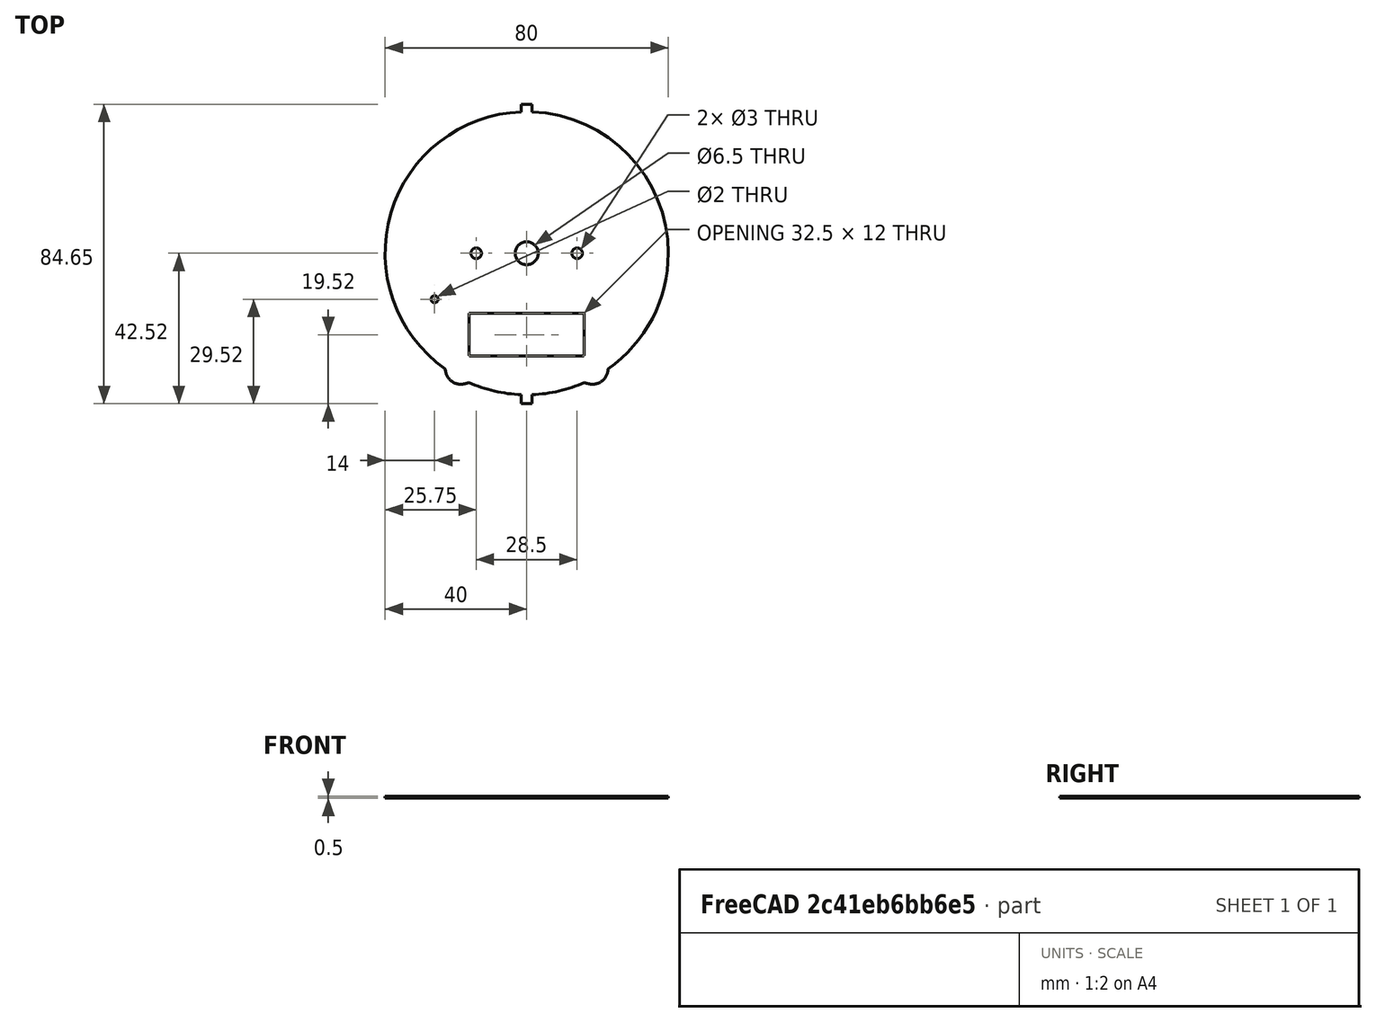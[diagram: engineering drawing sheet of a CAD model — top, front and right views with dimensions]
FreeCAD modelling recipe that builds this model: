
FCSTD DOCUMENT  (FreeCAD 1.0R39285 (Git))
Label: Tach_Face_Reference_CAD_Model
License: All rights reserved
LicenseURL: http://en.wikipedia.org/wiki/All_rights_reserved
objects: TechDraw::DrawViewDimension×17, Sketcher::SketchObject×6, PartDesign::Pad×3, PartDesign::Pocket×3, TechDraw::DrawProjGroupItem×2, Image::ImagePlane×1, PartDesign::Body×1, TechDraw::DrawSVGTemplate×1, TechDraw::DrawProjGroup×1, TechDraw::DrawViewAnnotation×1, TechDraw::DrawPage×1
note: 57 computed .brp shape members not serialized (recipe doc carries the construction recipe); baked Part::Feature solids carry a one-line shape summary decoded from their .brp

FEATURE [Sketcher::SketchObject] Sketch  label="Square Hole"
  ArcFitTolerance = 1e-06
  AttachmentSupport = -> [XY_Plane]
  FullyConstrained = true
  MakeInternals = false
  MapMode = 5
  sketch-geometry (5):
    g0: LineSegment StartX=-16.25 StartY=-29 StartZ=0 EndX=16.25 EndY=-29 EndZ=0
    g1: LineSegment StartX=16.25 StartY=-29 StartZ=0 EndX=16.25 EndY=-17 EndZ=0
    g2: LineSegment StartX=16.25 StartY=-17 StartZ=0 EndX=-16.25 EndY=-17 EndZ=0
    g3: LineSegment StartX=-16.25 StartY=-17 StartZ=0 EndX=-16.25 EndY=-29 EndZ=0
    g4: LineSegment [constr] StartX=0 StartY=0 StartZ=0 EndX=0 EndY=-17 EndZ=0
  constraints (14):
    c: Coincident(g1,g0)
    c: Vertical(g1)
    c: Coincident(g2,g1)
    c: Horizontal(g2)
    c: Coincident(g3,g2)
    c: Coincident(g3,g0)
    c: Vertical(g3)
    c: Horizontal(g0)
    c: Coincident(g4,g-1)
    c: DistanceY(g4,g4) = 17
    c: PointOnObject(g4,g2)
    c: Symmetric(g2,g1,g4)
    c: DistanceX(g0,g0) = 32.5
    c: DistanceY(g1,g1) = 12
FEATURE [Sketcher::SketchObject] Sketch001  label="Main Body"
  ArcFitTolerance = 1e-06
  AttachmentSupport = -> [XY_Plane]
  FullyConstrained = true
  MakeInternals = false
  MapMode = 5
  sketch-geometry (1):
    g0: Circle CenterX=0 CenterY=0 CenterZ=0 NormalX=0 NormalY=0 NormalZ=1 AngleXU=0 Radius=40
  constraints (2):
    c: Coincident(g-1,g0)
    c: Diameter(g0) = 80
FEATURE [Image::ImagePlane] Tach_Face_Reference_Image
  Placement = pos=(-3,-9,0) rot=(0,0,1;0rad)
  XSize = 229.908
  YSize = 172.431
FEATURE [PartDesign::Pad] Pad
  Direction = (0,0,1)
  Length = 0.5
  Length2 = 10
  Profile = -> Sketch001
  ReferenceAxis = -> Sketch001 [N_Axis]
  Suppressed = false
  Type = 0
FEATURE [PartDesign::Pocket] Pocket  label="Square_Hole"
  BaseFeature = -> Pad
  Direction = (0,0,-1)
  Length = 5
  Length2 = 5
  Profile = -> Sketch
  ReferenceAxis = -> Sketch [N_Axis]
  Reversed = true
  Suppressed = false
  Type = 1
FEATURE [Sketcher::SketchObject] Sketch002
  ArcFitTolerance = 1e-06
  AttachmentSupport = -> [XY_Plane]
  FullyConstrained = true
  MakeInternals = false
  MapMode = 5
  sketch-geometry (5):
    g0: Circle CenterX=0 CenterY=0 CenterZ=0 NormalX=0 NormalY=0 NormalZ=1 AngleXU=0 Radius=3.25
    g1: LineSegment [constr] StartX=0 StartY=0 StartZ=0 EndX=14.25 EndY=0 EndZ=0
    g2: Circle CenterX=14.25 CenterY=0 CenterZ=0 NormalX=0 NormalY=0 NormalZ=1 AngleXU=0 Radius=1.5
    g3: LineSegment [constr] StartX=0 StartY=0 StartZ=0 EndX=-14.25 EndY=0 EndZ=0
    g4: Circle CenterX=-14.25 CenterY=0 CenterZ=0 NormalX=0 NormalY=0 NormalZ=1 AngleXU=0 Radius=1.5
  constraints (12):
    c: Coincident(g0,g-1)
    c: Diameter(g0) = 6.5
    c: Coincident(g1,g0)
    c: PointOnObject(g1,g-1)
    c: Coincident(g2,g1)
    c: DistanceX(g1,g1) = 14.25
    c: Diameter(g2) = 3
    c: Coincident(g3,g0)
    c: PointOnObject(g3,g-1)
    c: Coincident(g4,g3)
    c: Diameter(g4) = 3
    c: DistanceX(g3,g3) = 14.25
FEATURE [PartDesign::Pocket] Pocket001  label="Needle_Hole"
  BaseFeature = -> Pocket
  Direction = (0,0,-1)
  Length = 5
  Length2 = 5
  Profile = -> Sketch002
  ReferenceAxis = -> Sketch002 [N_Axis]
  Reversed = true
  Suppressed = false
  Type = 1
FEATURE [Sketcher::SketchObject] Sketch003
  ArcFitTolerance = 1e-06
  AttachmentSupport = -> [XY_Plane]
  FullyConstrained = true
  MakeInternals = false
  MapMode = 5
  sketch-geometry (3):
    g0: LineSegment [constr] StartX=0 StartY=0 StartZ=0 EndX=-26 EndY=0 EndZ=0
    g1: LineSegment [constr] StartX=-26 StartY=0 StartZ=0 EndX=-26 EndY=-13 EndZ=0
    g2: Circle CenterX=-26 CenterY=-13 CenterZ=0 NormalX=0 NormalY=0 NormalZ=1 AngleXU=0 Radius=1
  constraints (8):
    c: Coincident(g0,g-1)
    c: PointOnObject(g0,g-1)
    c: Coincident(g1,g0)
    c: Vertical(g1)
    c: Coincident(g2,g1)
    c: Diameter(g2) = 2
    c: DistanceY(g1,g1) = 13
    c: DistanceX(g0,g0) = 26
FEATURE [PartDesign::Pocket] Pocket002  label="Needle_Start_Point"
  BaseFeature = -> Pocket001
  Direction = (0,0,-1)
  Length = 5
  Length2 = 5
  Profile = -> Sketch003
  ReferenceAxis = -> Sketch003 [N_Axis]
  Reversed = true
  Suppressed = false
  Type = 1
FEATURE [Sketcher::SketchObject] Sketch004
  ArcFitTolerance = 1e-06
  AttachmentSupport = -> [XY_Plane]
  FullyConstrained = true
  MakeInternals = false
  MapMode = 5
  sketch-geometry (10):
    g0: LineSegment StartX=-1.5 StartY=-42.52 StartZ=0 EndX=1.5 EndY=-42.52 EndZ=0
    g1: LineSegment StartX=1.5 StartY=-42.52 StartZ=0 EndX=1.5 EndY=-39.1 EndZ=0
    g2: LineSegment StartX=1.5 StartY=-39.1 StartZ=0 EndX=-1.5 EndY=-39.1 EndZ=0
    g3: LineSegment StartX=-1.5 StartY=-39.1 StartZ=0 EndX=-1.5 EndY=-42.52 EndZ=0
    g4: LineSegment [constr] StartX=0 StartY=0 StartZ=0 EndX=0 EndY=-39.1 EndZ=0
    g5: LineSegment StartX=-1.5 StartY=42.13 StartZ=0 EndX=-1.5 EndY=39.22 EndZ=0
    g6: LineSegment StartX=-1.5 StartY=39.22 StartZ=0 EndX=1.5 EndY=39.22 EndZ=0
    g7: LineSegment StartX=1.5 StartY=39.22 StartZ=0 EndX=1.5 EndY=42.13 EndZ=0
    g8: LineSegment StartX=1.5 StartY=42.13 StartZ=0 EndX=-1.5 EndY=42.13 EndZ=0
    g9: LineSegment [constr] StartX=0 StartY=0 StartZ=0 EndX=0 EndY=39.22 EndZ=0
  constraints (28):
    c: Coincident(g0,g1)
    c: Coincident(g1,g2)
    c: Coincident(g2,g3)
    c: Coincident(g3,g0)
    c: Horizontal(g0)
    c: Horizontal(g2)
    c: Vertical(g1)
    c: Vertical(g3)
    c: Coincident(g4,g-1)
    c: Symmetric(g2,g2,g4)
    c: Vertical(g4)
    c: DistanceY(g1,g1) = 3.42
    c: DistanceY(g4,g4) = 39.1
    c: DistanceX(g0,g0) = 3
    c: Coincident(g5,g6)
    c: Coincident(g6,g7)
    c: Coincident(g7,g8)
    c: Coincident(g8,g5)
    c: Vertical(g5)
    c: Vertical(g7)
    c: Horizontal(g6)
    c: Horizontal(g8)
    c: Coincident(g9,g4)
    c: Symmetric(g6,g6,g9)
    c: Vertical(g9)
    c: DistanceX(g8,g8) = 3
    c: DistanceY(g7,g7) = 2.91
    c: DistanceY(g9,g9) = 39.22
FEATURE [PartDesign::Pad] Pad001  label="Line_Up_Tabs"
  BaseFeature = -> Pocket002
  Direction = (0,0,1)
  Length = 0.5
  Length2 = 10
  Profile = -> Sketch004
  ReferenceAxis = -> Sketch004 [N_Axis]
  Refine = true
  Suppressed = false
  Type = 0
FEATURE [Sketcher::SketchObject] Sketch005
  ArcFitTolerance = 1e-06
  AttachmentSupport = -> [XY_Plane]
  FullyConstrained = true
  MakeInternals = false
  MapMode = 5
  sketch-geometry (4):
    g0: Circle CenterX=18.565 CenterY=-32.63 CenterZ=0 NormalX=0 NormalY=0 NormalZ=1 AngleXU=0 Radius=4.42
    g1: Circle CenterX=-18.565 CenterY=-32.63 CenterZ=0 NormalX=0 NormalY=0 NormalZ=1 AngleXU=0 Radius=4.42
    g2: LineSegment [constr] StartX=-18.565 StartY=-32.63 StartZ=0 EndX=18.565 EndY=-32.63 EndZ=0
    g3: LineSegment [constr] StartX=0 StartY=0 StartZ=0 EndX=0 EndY=-32.63 EndZ=0
  constraints (10):
    c: Coincident(g2,g0)
    c: Horizontal(g2)
    c: Coincident(g3,g-1)
    c: Symmetric(g2,g2,g3)
    c: Vertical(g3)
    c: Coincident(g1,g2)
    c: Equal(g1,g0)
    c: Diameter(g1) = 8.84
    c: DistanceY(g3,g3) = 32.63
    c: DistanceX(g2,g2) = 37.13
FEATURE [PartDesign::Pad] Pad002  label="Line_Up_Curves"
  BaseFeature = -> Pad001
  Direction = (0,0,1)
  Length = 0.5
  Length2 = 10
  Profile = -> Sketch005
  ReferenceAxis = -> Sketch005 [N_Axis]
  Refine = true
  Suppressed = false
  Type = 0
FEATURE [PartDesign::Body] Body
  AllowCompound = false
  Group = -> [Sketch,Sketch001,Pad,Pocket,Sketch002,Pocket001,Sketch003,Pocket002,Sketch004,Pad001,Sketch005,Pad002]
  Origin = -> Origin
  Tip = -> Pad002
FEATURE [TechDraw::DrawSVGTemplate] Template
  Height = 210
  Orientation = 1
  Template = <userpath>/AppData/Local/Programs/FreeCAD 1.0/data/Mod/TechDraw/Templates/Default_Template_A4_Landscape.svg
  Width = 297
FEATURE [TechDraw::DrawProjGroupItem] View  label="Front"
  CoarseView = false
  Direction = (0,0,1)
  Focus = 100
  HardHidden = false
  IsoCount = 0
  IsoHidden = false
  IsoVisible = false
  LockPosition = true
  Perspective = false
  Rotation = 0
  RotationVector = (1,0,0)
  Scale = 2
  ScaleType = 2
  ScrubCount = 1
  SeamHidden = false
  SeamVisible = false
  SmoothHidden = false
  SmoothVisible = true
  Source = -> [Body]
  Type = 0
  X = 0
  XDirection = (1,-2e-16,0)
  Y = 0
FEATURE [TechDraw::DrawViewDimension] Dimension002
  AngleOverride = false
  Arbitrary = false
  ArbitraryTolerances = false
  BoxCorners = (2) [(-80,-84.65,0),(80,84.65,0)]
  EqualTolerance = true
  ExtensionAngle = 0
  FormatSpec = ⌀%.2w
  FormatSpecOverTolerance = %+.2w
  FormatSpecUnderTolerance = %+.2w
  Inverted = false
  LineAngle = 0
  LockPosition = false
  MeasureType = 1
  OverTolerance = 0
  References2D = -> [View]
  Rotation = 0
  ScaleType = 0
  TheoreticalExact = false
  Type = 5
  UnderTolerance = 0
  X = 42.0799
  Y = 18.6943
FEATURE [TechDraw::DrawViewDimension] Dimension003
  AngleOverride = false
  Arbitrary = false
  ArbitraryTolerances = false
  BoxCorners = (2) [(-80,-84.65,0),(80,84.65,0)]
  EqualTolerance = true
  ExtensionAngle = 0
  FormatSpec = ⌀%.2w
  FormatSpecOverTolerance = %+.2w
  FormatSpecUnderTolerance = %+.2w
  Inverted = false
  LineAngle = 0
  LockPosition = false
  MeasureType = 1
  OverTolerance = 0
  References2D = -> [View]
  Rotation = 0
  ScaleType = 0
  TheoreticalExact = false
  Type = 5
  UnderTolerance = 0
  X = 17.8416
  Y = 21.7678
FEATURE [TechDraw::DrawViewDimension] Dimension004
  AngleOverride = false
  Arbitrary = false
  ArbitraryTolerances = false
  BoxCorners = (2) [(-80,-84.65,0),(80,84.65,0)]
  EqualTolerance = true
  ExtensionAngle = 0
  FormatSpec = R%.2w
  FormatSpecOverTolerance = %+.2w
  FormatSpecUnderTolerance = %+.2w
  Inverted = false
  LineAngle = 0
  LockPosition = false
  MeasureType = 1
  OverTolerance = 0
  References2D = -> [View]
  Rotation = 0
  ScaleType = 0
  TheoreticalExact = false
  Type = 4
  UnderTolerance = 0
  X = -31.2665
  Y = 28.5071
FEATURE [TechDraw::DrawViewDimension] Dimension005
  AngleOverride = false
  Arbitrary = false
  ArbitraryTolerances = false
  BoxCorners = (2) [(-80,-84.65,0),(80,84.65,0)]
  EqualTolerance = true
  ExtensionAngle = 0
  FormatSpec = %.2w
  FormatSpecOverTolerance = %+.2w
  FormatSpecUnderTolerance = %+.2w
  Inverted = false
  LineAngle = 0
  LockPosition = false
  MeasureType = 1
  OverTolerance = 0
  References2D = -> [View]
  Rotation = 0
  ScaleType = 0
  TheoreticalExact = false
  Type = 0
  UnderTolerance = 0
  X = -14.25
  Y = -7.52715
FEATURE [TechDraw::DrawViewDimension] Dimension006
  AngleOverride = false
  Arbitrary = false
  ArbitraryTolerances = false
  BoxCorners = (2) [(-80,-84.65,0),(80,84.65,0)]
  EqualTolerance = true
  ExtensionAngle = 0
  FormatSpec = %.2w
  FormatSpecOverTolerance = %+.2w
  FormatSpecUnderTolerance = %+.2w
  Inverted = false
  LineAngle = 0
  LockPosition = false
  MeasureType = 1
  OverTolerance = 0
  References2D = -> [View]
  Rotation = 0
  ScaleType = 0
  TheoreticalExact = false
  Type = 0
  UnderTolerance = 0
  X = -41.8511
  Y = -14.5271
FEATURE [TechDraw::DrawViewDimension] Dimension007
  AngleOverride = false
  Arbitrary = false
  ArbitraryTolerances = false
  BoxCorners = (2) [(-80,-84.65,0),(80,84.65,0)]
  EqualTolerance = true
  ExtensionAngle = 0
  FormatSpec = %.2w
  FormatSpecOverTolerance = %+.2w
  FormatSpecUnderTolerance = %+.2w
  Inverted = false
  LineAngle = 0
  LockPosition = false
  MeasureType = 1
  OverTolerance = 0
  References2D = -> [View]
  Rotation = 0
  ScaleType = 0
  TheoreticalExact = false
  Type = 0
  UnderTolerance = 0
  X = 80.457
  Y = -25.1436
FEATURE [TechDraw::DrawViewDimension] Dimension008
  AngleOverride = false
  Arbitrary = false
  ArbitraryTolerances = false
  BoxCorners = (2) [(-80,-84.65,0),(80,84.65,0)]
  EqualTolerance = true
  ExtensionAngle = 0
  FormatSpec = %.2w
  FormatSpecOverTolerance = %+.2w
  FormatSpecUnderTolerance = %+.2w
  Inverted = false
  LineAngle = 0
  LockPosition = false
  MeasureType = 1
  OverTolerance = 0
  References2D = -> [View]
  Rotation = 0
  ScaleType = 0
  TheoreticalExact = false
  Type = 0
  UnderTolerance = 0
  X = 91.7896
  Y = -17.7435
FEATURE [TechDraw::DrawViewDimension] Dimension009
  AngleOverride = false
  Arbitrary = false
  ArbitraryTolerances = false
  BoxCorners = (2) [(-80,-84.65,0),(80,84.65,0)]
  EqualTolerance = true
  ExtensionAngle = 0
  FormatSpec = %.2w
  FormatSpecOverTolerance = %+.2w
  FormatSpecUnderTolerance = %+.2w
  Inverted = false
  LineAngle = 0
  LockPosition = false
  MeasureType = 1
  OverTolerance = 0
  References2D = -> [View]
  Rotation = 0
  ScaleType = 0
  TheoreticalExact = false
  Type = 0
  UnderTolerance = 0
  X = -56.1876
  Y = -12.61
FEATURE [TechDraw::DrawViewDimension] Dimension010
  AngleOverride = false
  Arbitrary = false
  ArbitraryTolerances = false
  BoxCorners = (2) [(-80,-84.65,0),(80,84.65,0)]
  EqualTolerance = true
  ExtensionAngle = 0
  FormatSpec = %.2w
  FormatSpecOverTolerance = %+.2w
  FormatSpecUnderTolerance = %+.2w
  Inverted = false
  LineAngle = 0
  LockPosition = false
  MeasureType = 1
  OverTolerance = 0
  References2D = -> [View]
  Rotation = 0
  ScaleType = 0
  TheoreticalExact = false
  Type = 0
  UnderTolerance = 0
  X = 95.3564
  Y = 67.5126
FEATURE [TechDraw::DrawViewDimension] Dimension011
  AngleOverride = false
  Arbitrary = false
  ArbitraryTolerances = false
  BoxCorners = (2) [(-80,-84.65,0),(80,84.65,0)]
  EqualTolerance = true
  ExtensionAngle = 0
  FormatSpec = %.2w
  FormatSpecOverTolerance = %+.2w
  FormatSpecUnderTolerance = %+.2w
  Inverted = false
  LineAngle = 0
  LockPosition = false
  MeasureType = 1
  OverTolerance = 0
  References2D = -> [View]
  Rotation = 0
  ScaleType = 0
  TheoreticalExact = false
  Type = 0
  UnderTolerance = 0
  X = 13.6408
  Y = 71.5109
FEATURE [TechDraw::DrawViewDimension] Dimension
  AngleOverride = false
  Arbitrary = false
  ArbitraryTolerances = false
  BoxCorners = (2) [(-80,-84.65,0),(80,84.65,0)]
  EqualTolerance = true
  ExtensionAngle = 0
  FormatSpec = %.2w
  FormatSpecOverTolerance = %+.2w
  FormatSpecUnderTolerance = %+.2w
  Inverted = false
  LineAngle = 0
  LockPosition = false
  MeasureType = 1
  OverTolerance = 0
  References2D = -> [View]
  Rotation = 0
  ScaleType = 0
  TheoreticalExact = false
  Type = 0
  UnderTolerance = 0
  X = -16.25
  Y = -24.2672
FEATURE [TechDraw::DrawViewDimension] Dimension012
  AngleOverride = false
  Arbitrary = false
  ArbitraryTolerances = false
  BoxCorners = (2) [(-80,-84.65,0),(80,84.65,0)]
  EqualTolerance = true
  ExtensionAngle = 0
  FormatSpec = ⌀%.2w
  FormatSpecOverTolerance = %+.2w
  FormatSpecUnderTolerance = %+.2w
  Inverted = false
  LineAngle = 0
  LockPosition = false
  MeasureType = 1
  OverTolerance = 0
  References2D = -> [View]
  Rotation = 0
  ScaleType = 0
  TheoreticalExact = false
  Type = 5
  UnderTolerance = 0
  X = -55.4804
  Y = -16.3113
FEATURE [TechDraw::DrawViewDimension] Dimension013
  AngleOverride = false
  Arbitrary = false
  ArbitraryTolerances = false
  BoxCorners = (2) [(-80,-84.65,0),(80,84.65,0)]
  EqualTolerance = true
  ExtensionAngle = 0
  FormatSpec = %.2w
  FormatSpecOverTolerance = %+.2w
  FormatSpecUnderTolerance = %+.2w
  Inverted = false
  LineAngle = 0
  LockPosition = false
  MeasureType = 1
  OverTolerance = 0
  References2D = -> [View]
  Rotation = 0
  ScaleType = 0
  TheoreticalExact = false
  Type = 0
  UnderTolerance = 0
  X = 104.379
  Y = -46.5238
FEATURE [TechDraw::DrawViewDimension] Dimension014
  AngleOverride = false
  Arbitrary = false
  ArbitraryTolerances = false
  BoxCorners = (2) [(-80,-84.65,0),(80,84.65,0)]
  EqualTolerance = true
  ExtensionAngle = 0
  FormatSpec = %.2w
  FormatSpecOverTolerance = %+.2w
  FormatSpecUnderTolerance = %+.2w
  Inverted = false
  LineAngle = 0
  LockPosition = false
  MeasureType = 1
  OverTolerance = 0
  References2D = -> [View]
  Rotation = 0
  ScaleType = 0
  TheoreticalExact = false
  Type = 0
  UnderTolerance = 0
  X = -13.4779
  Y = -59.7602
FEATURE [TechDraw::DrawViewDimension] Dimension015
  AngleOverride = false
  Arbitrary = false
  ArbitraryTolerances = false
  BoxCorners = (2) [(-80,-84.65,0),(80,84.65,0)]
  EqualTolerance = true
  ExtensionAngle = 0
  FormatSpec = ⌀%.2w
  FormatSpecOverTolerance = %+.2w
  FormatSpecUnderTolerance = %+.2w
  Inverted = false
  LineAngle = 0
  LockPosition = false
  MeasureType = 1
  OverTolerance = 0
  References2D = -> [View]
  Rotation = 0
  ScaleType = 0
  TheoreticalExact = false
  Type = 5
  UnderTolerance = 0
  X = -42.609
  Y = 15.3389
FEATURE [TechDraw::DrawProjGroupItem] ProjItem  label="Left"
  CoarseView = false
  Direction = (-1,2e-16,1e-16)
  Focus = 100
  HardHidden = false
  IsoCount = 0
  IsoHidden = false
  IsoVisible = false
  LockPosition = false
  Perspective = false
  Rotation = 0
  RotationVector = (1,0,0)
  ScaleType = 0
  ScrubCount = 1
  SeamHidden = false
  SeamVisible = false
  SmoothHidden = false
  SmoothVisible = true
  Source = -> [Body]
  Type = 1
  X = 118.961
  XDirection = (1e-16,0,1)
  Y = 0
FEATURE [TechDraw::DrawProjGroup] ProjGroup
  Anchor = -> View
  AutoDistribute = true
  LockPosition = false
  ProjectionType = 0
  Rotation = 0
  Scale = 2
  ScaleType = 2
  Source = -> [Body]
  Views = -> [View,ProjItem]
  X = 117.136
  Y = 98.2432
  spacingX = 15
  spacingY = 15
FEATURE [TechDraw::DrawViewDimension] Dimension016
  AngleOverride = false
  Arbitrary = false
  ArbitraryTolerances = false
  BoxCorners = (2) [(-0.5,-84.65,-1e-07),(0.5,84.65,1e-07)]
  EqualTolerance = true
  ExtensionAngle = 0
  FormatSpec = %.2w
  FormatSpecOverTolerance = %+.2w
  FormatSpecUnderTolerance = %+.2w
  Inverted = false
  LineAngle = 0
  LockPosition = false
  MeasureType = 1
  OverTolerance = 0
  References2D = -> [ProjItem]
  Rotation = 0
  ScaleType = 0
  TheoreticalExact = false
  Type = 0
  UnderTolerance = 0
  X = 24.8754
  Y = 33.0055
FEATURE [TechDraw::DrawViewDimension] Dimension017
  AngleOverride = false
  Arbitrary = false
  ArbitraryTolerances = false
  BoxCorners = (2) [(-80,-84.65,0),(80,84.65,0)]
  EqualTolerance = true
  ExtensionAngle = 0
  FormatSpec = R%.2w
  FormatSpecOverTolerance = %+.2w
  FormatSpecUnderTolerance = %+.2w
  Inverted = false
  LineAngle = 0
  LockPosition = false
  MeasureType = 1
  OverTolerance = 0
  References2D = -> [View]
  Rotation = 0
  ScaleType = 0
  TheoreticalExact = false
  Type = 4
  UnderTolerance = 0
  X = 69.0127
  Y = -77.6037
FEATURE [TechDraw::DrawViewAnnotation] Annotation
  Font = osifont
  LineSpace = 100
  LockPosition = false
  MaxWidth = -1
  Rotation = 0
  ScaleType = 0
  Text = Tech Drawing of Gauge Face
  TextSize = 5
  TextStyle = 0
  X = 155.027
  Y = 200.628
FEATURE [TechDraw::DrawPage] Page  label="Tech_drawing"
  KeepUpdated = true
  NextBalloonIndex = 2
  ProjectionType = 0
  Template = -> Template
  Views = -> [Dimension002,Dimension003,Dimension004,Dimension005,Dimension006,Dimension007,Dimension008,Dimension009,Dimension010,Dimension011,Dimension,Dimension012,Dimension013,Dimension014,Dimension015,ProjGroup,Dimension016,Dimension017,Annotation]
